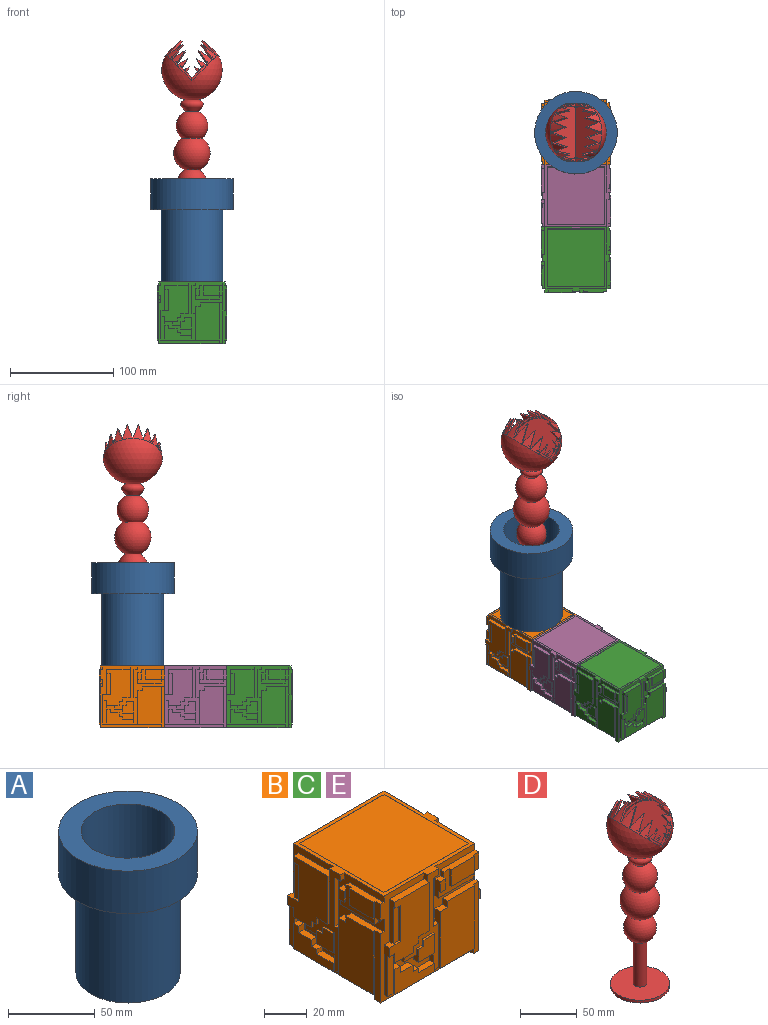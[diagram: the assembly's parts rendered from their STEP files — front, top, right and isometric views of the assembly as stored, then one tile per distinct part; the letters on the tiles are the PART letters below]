
ASSEMBLY  parts=5 mates=3
PART A: 7 faces, bbox 80x80x100 mm
  f0: cylinder r=27mm len=98mm, axis (0,0,1), area 16625.3mm2, adj f3,f6
  f1: cylinder r=40mm len=80mm, axis (0,0,1), area 7539.8mm2, adj f2,f3
  f2: plane 80x80mm, normal (0,0,-1), area 2199.1mm2, adj f1,f4
  f3: plane 80x80mm, normal (0,0,1), area 2736.3mm2, adj f0,f1
  f4: cylinder r=30mm len=70mm, axis (0,0,1), area 13194.7mm2, adj f2,f5
  f5: plane 60x60mm, normal (0,0,-1), area 2827.4mm2, adj f4
  f6: plane 54x54mm, normal (0,0,1), area 2290.2mm2, adj f0
PART B: 229 faces, bbox 67.2x63.6x60 mm
  f0: plane 64.8x62.4mm, normal (0,0,1), area 515.8mm2, adj f3,f4,f8,f9,f10,f60,f64,f67
  f1: plane 56.4x3.6mm, normal (-1,0,0), area 203mm2, adj f2,f81,f165,f210
  f2: plane 64.8x62.4mm, normal (0,0,-1), area 3625.9mm2, adj f1,f9,f10,f71,f72,f81,f142,f143
  f3: plane 27.97x26.4mm, normal (-1,0,0), area 182.8mm2, adj f0,f81,f157,f158,f161,f199
  f4: plane 31.2x30mm, normal (-1,0,0), area 331.7mm2, adj f0,f9,f149,f183,f184,f185,f186,f190
  f5: plane 3.6x2.4mm, normal (1,0,0), area 8.6mm2, adj f8,f69,f70,f75
  f6: plane 26.4x13.32mm, normal (0,-1,0), area 146.1mm2, adj f12,f28,f29,f30,f31,f32,f33,f34
  f7: plane 14.4x1.2mm, normal (-1,0,0), area 17.3mm2, adj f26,f34,f35,f74
  f8: plane 31.2x30mm, normal (0,-1,0), area 331.7mm2, adj f0,f5,f10,f44,f45,f46,f47,f51
  f9: plane 60x58.8mm, normal (0,-1,0), area 503.9mm2, adj f0,f2,f4,f11,f18,f19,f22,f26
  f10: plane 60x58.8mm, normal (1,0,0), area 503.9mm2, adj f0,f2,f8,f44,f51,f72,f75,f76
  f11: plane 28.43x3.6mm, normal (-1,0,0), area 74.5mm2, adj f9,f22,f23,f25,f26,f74
  f12: plane 12x3.6mm, normal (0,0,-1), area 31.7mm2, adj f6,f13,f24,f25,f65,f67,f73
  f13: plane 3.6x1.2mm, normal (1,0,0), area 4.3mm2, adj f12,f14,f25,f67
  f14: plane 3.6x1.2mm, normal (0,0,-1), area 4.3mm2, adj f13,f15,f25,f67
  f15: plane 3.6x1.2mm, normal (1,0,0), area 4.3mm2, adj f14,f16,f25,f67
  f16: plane 7.2x1.2mm, normal (0,0,-1), area 8.6mm2, adj f15,f17,f25,f67
  f17: plane 27.6x1.2mm, normal (1,0,0), area 33.1mm2, adj f16,f18,f25,f67
  f18: plane 22.8x3.6mm, normal (0,0,1), area 82.1mm2, adj f9,f17,f19,f25,f60
  f19: plane 24.37x3.6mm, normal (-1,0,0), area 62.8mm2, adj f9,f18,f20,f22,f25,f77
  f20: plane 3.6x1.2mm, normal (0,0,-1), area 4.3mm2, adj f19,f21,f25,f77
  f21: plane 20.77x1.2mm, normal (-1,0,0), area 24.9mm2, adj f20,f22,f25,f77
  f22: plane 7.2x3.6mm, normal (0,0,1), area 17.3mm2, adj f9,f11,f19,f21,f25,f77
  f23: plane 3.6x1.2mm, normal (0,0,-1), area 4.3mm2, adj f11,f24,f25,f74
  f24: plane 5.22x1.2mm, normal (-1,0,0), area 6.3mm2, adj f12,f23,f25,f74
  f25: plane 34.8x26.4mm, normal (0,-1,0), area 672.7mm2, adj f11,f12,f13,f14,f15,f16,f17,f18
  f26: plane 56.4x3.6mm, normal (0,0,-1), area 194.4mm2, adj f7,f9,f11,f27,f35,f43,f47,f48
  f27: plane 4.68x1.2mm, normal (1,0,0), area 5.6mm2, adj f26,f28,f35,f67
  f28: plane 10.8x3.6mm, normal (0,0,1), area 38.9mm2, adj f6,f27,f29,f35,f59
  f29: plane 3.6x2.52mm, normal (1,0,0), area 9.1mm2, adj f6,f28,f30,f35
  f30: plane 3.6x3.6mm, normal (0,0,1), area 13mm2, adj f6,f29,f31,f35
  f31: plane 3.6x3.6mm, normal (1,0,0), area 13mm2, adj f6,f30,f32,f35
  f32: plane 8.4x3.6mm, normal (0,0,1), area 30.2mm2, adj f6,f31,f33,f35
  f33: plane 3.6x3.6mm, normal (1,0,0), area 13mm2, adj f6,f32,f34,f35
  f34: plane 3.6x3.6mm, normal (0,0,1), area 13mm2, adj f6,f7,f33,f35,f73
  f35: plane 26.4x14.4mm, normal (0,-1,0), area 219.1mm2, adj f7,f26,f27,f28,f29,f30,f31,f32
  f36: plane 7.4x3.6mm, normal (-1,0,0), area 18mm2, adj f6,f37,f41,f42,f66,f67
  f37: plane 10.8x3.6mm, normal (0,0,-1), area 38.9mm2, adj f6,f36,f38,f42,f59
  f38: plane 11x1.2mm, normal (1,0,0), area 13.2mm2, adj f37,f39,f42,f67
  f39: plane 7.2x1.2mm, normal (0,0,1), area 8.6mm2, adj f38,f40,f42,f67
  f40: plane 3.6x1.2mm, normal (-1,0,0), area 4.3mm2, adj f39,f41,f42,f67
  f41: plane 3.6x1.2mm, normal (0,0,1), area 4.3mm2, adj f36,f40,f42,f67
  f42: plane 11x10.8mm, normal (0,-1,0), area 105.8mm2, adj f36,f37,f38,f39,f40,f41
  f43: plane 36x1.2mm, normal (1,0,0), area 43.2mm2, adj f26,f44,f48,f72
  f44: plane 21.6x3.6mm, normal (0,0,1), area 73.4mm2, adj f8,f10,f43,f45,f48,f72
  f45: plane 3.6x3.6mm, normal (-1,0,0), area 13mm2, adj f8,f44,f46,f48
  f46: plane 4.8x3.6mm, normal (0,0,1), area 17.3mm2, adj f8,f45,f47,f48
  f47: plane 32.4x3.6mm, normal (-1,0,0), area 56.2mm2, adj f8,f26,f46,f48,f61,f67
  f48: plane 36x22.8mm, normal (0,-1,0), area 803.5mm2, adj f26,f43,f44,f45,f46,f47
  f49: plane 15.6x1.2mm, normal (0,0,-1), area 18.7mm2, adj f50,f52,f53,f70
  f50: plane 9.6x1.2mm, normal (1,0,0), area 11.5mm2, adj f49,f51,f53,f76
  f51: plane 22.8x3.6mm, normal (0,0,1), area 73.4mm2, adj f8,f10,f50,f52,f53,f68,f70,f76
  f52: plane 9.6x1.2mm, normal (-1,0,0), area 11.5mm2, adj f49,f51,f53,f70
  f53: plane 15.6x9.6mm, normal (0,-1,0), area 149.8mm2, adj f49,f50,f51,f52
  f54: plane 3.6x1.2mm, normal (0,0,-1), area 4.3mm2, adj f55,f57,f58,f70
  f55: plane 6.25x1.2mm, normal (1,0,0), area 7.5mm2, adj f54,f56,f58,f70
  f56: plane 3.6x3.6mm, normal (0,0,1), area 13mm2, adj f8,f55,f57,f58,f68
  f57: plane 9.85x3.6mm, normal (-1,0,0), area 31.1mm2, adj f8,f54,f56,f58,f69,f70
  f58: plane 6.25x3.6mm, normal (0,-1,0), area 22.5mm2, adj f54,f55,f56,f57
  f59: plane 5.92x2.4mm, normal (-1,0,0), area 14.2mm2, adj f6,f28,f37,f67
  f60: plane 3.6x2.4mm, normal (-1,0,0), area 8.6mm2, adj f0,f9,f18,f67
  f61: plane 3.6x2.4mm, normal (0,0,1), area 8.6mm2, adj f8,f47,f62,f67
  f62: plane 27.6x2.4mm, normal (1,0,0), area 66.2mm2, adj f8,f61,f63,f67
  f63: plane 3.6x2.4mm, normal (0,0,-1), area 8.6mm2, adj f8,f62,f64,f67
  f64: plane 3.6x2.4mm, normal (1,0,0), area 8.6mm2, adj f0,f8,f63,f67
  f65: plane 3.6x2.4mm, normal (-1,0,0), area 8.6mm2, adj f6,f12,f66,f67
  f66: plane 8.38x2.4mm, normal (0,0,-1), area 20.1mm2, adj f6,f36,f65,f67
  f67: plane 56.4x22.78mm, normal (0,-1,0), area 311mm2, adj f0,f12,f13,f14,f15,f16,f17,f26
  f68: plane 3.35x2.4mm, normal (-1,0,0), area 8mm2, adj f8,f51,f56,f70
  f69: plane 22.8x2.4mm, normal (0,0,-1), area 54.7mm2, adj f5,f8,f57,f70
  f70: plane 22.8x13.2mm, normal (0,-1,0), area 116.6mm2, adj f5,f49,f51,f52,f54,f55,f57,f68
  f71: plane 3.6x2.4mm, normal (-1,0,0), area 8.6mm2, adj f2,f9,f26,f72
  f72: plane 39.6x3.6mm, normal (0,-1,0), area 142.6mm2, adj f2,f10,f43,f44,f71
  f73: plane 3.6x2.4mm, normal (1,0,0), area 8.6mm2, adj f6,f12,f34,f74
  f74: plane 23.22x3.6mm, normal (0,-1,0), area 83.6mm2, adj f7,f11,f23,f24,f26,f73
  f75: plane 3.6x2.4mm, normal (0,0,-1), area 8.6mm2, adj f5,f8,f10,f76
  f76: plane 9.6x3.6mm, normal (0,-1,0), area 34.6mm2, adj f10,f50,f51,f75
  f77: plane 20.77x3.6mm, normal (0,-1,0), area 74.8mm2, adj f19,f20,f21,f22
  f78: plane 3.6x2.4mm, normal (0,1,0), area 8.6mm2, adj f80,f140,f141,f146
  f79: plane 14.4x1.2mm, normal (0,-1,0), area 17.3mm2, adj f97,f105,f106,f145
  f80: plane 31.2x30mm, normal (1,0,0), area 331.7mm2, adj f0,f78,f81,f115,f116,f117,f118,f122
  f81: plane 66x60mm, normal (0,1,0), area 3792.6mm2, adj f0,f1,f2,f3,f80,f115,f122,f143
  f82: plane 28.43x3.6mm, normal (0,-1,0), area 74.5mm2, adj f10,f93,f94,f96,f97,f145
  f83: plane 12x3.6mm, normal (0,0,-1), area 31.7mm2, adj f84,f95,f96,f136,f138,f144,f218
  f84: plane 3.6x1.2mm, normal (0,1,0), area 4.3mm2, adj f83,f85,f96,f138
  f85: plane 3.6x1.2mm, normal (0,0,-1), area 4.3mm2, adj f84,f86,f96,f138
  f86: plane 3.6x1.2mm, normal (0,1,0), area 4.3mm2, adj f85,f87,f96,f138
  f87: plane 7.2x1.2mm, normal (0,0,-1), area 8.6mm2, adj f86,f88,f96,f138
  f88: plane 27.6x1.2mm, normal (0,1,0), area 33.1mm2, adj f87,f89,f96,f138
  f89: plane 22.8x3.6mm, normal (0,0,1), area 82.1mm2, adj f10,f88,f90,f96,f131
  f90: plane 24.37x3.6mm, normal (0,-1,0), area 62.8mm2, adj f10,f89,f91,f93,f96,f148
  f91: plane 3.6x1.2mm, normal (0,0,-1), area 4.3mm2, adj f90,f92,f96,f148
  f92: plane 20.77x1.2mm, normal (0,-1,0), area 24.9mm2, adj f91,f93,f96,f148
  f93: plane 7.2x3.6mm, normal (0,0,1), area 17.3mm2, adj f10,f82,f90,f92,f96,f148
  f94: plane 3.6x1.2mm, normal (0,0,-1), area 4.3mm2, adj f82,f95,f96,f145
  f95: plane 5.22x1.2mm, normal (0,-1,0), area 6.3mm2, adj f83,f94,f96,f145
  f96: plane 34.8x26.4mm, normal (1,0,0), area 672.7mm2, adj f82,f83,f84,f85,f86,f87,f88,f89
  f97: plane 56.4x3.6mm, normal (0,0,-1), area 194.4mm2, adj f10,f79,f82,f98,f106,f114,f118,f119
  f98: plane 4.68x1.2mm, normal (0,1,0), area 5.6mm2, adj f97,f99,f106,f138
  f99: plane 10.8x3.6mm, normal (0,0,1), area 38.9mm2, adj f98,f100,f106,f130,f218
  f100: plane 3.6x2.52mm, normal (0,1,0), area 9.1mm2, adj f99,f101,f106,f218
  f101: plane 3.6x3.6mm, normal (0,0,1), area 13mm2, adj f100,f102,f106,f218
  f102: plane 3.6x3.6mm, normal (0,1,0), area 13mm2, adj f101,f103,f106,f218
  f103: plane 8.4x3.6mm, normal (0,0,1), area 30.2mm2, adj f102,f104,f106,f218
  f104: plane 3.6x3.6mm, normal (0,1,0), area 13mm2, adj f103,f105,f106,f218
  f105: plane 3.6x3.6mm, normal (0,0,1), area 13mm2, adj f79,f104,f106,f144,f218
  f106: plane 26.4x14.4mm, normal (1,0,0), area 219.1mm2, adj f79,f97,f98,f99,f100,f101,f102,f103
  f107: plane 7.4x3.6mm, normal (0,-1,0), area 18mm2, adj f108,f112,f113,f137,f138,f218
  f108: plane 10.8x3.6mm, normal (0,0,-1), area 38.9mm2, adj f107,f109,f113,f130,f218
  f109: plane 11x1.2mm, normal (0,1,0), area 13.2mm2, adj f108,f110,f113,f138
  f110: plane 7.2x1.2mm, normal (0,0,1), area 8.6mm2, adj f109,f111,f113,f138
  f111: plane 3.6x1.2mm, normal (0,-1,0), area 4.3mm2, adj f110,f112,f113,f138
  f112: plane 3.6x1.2mm, normal (0,0,1), area 4.3mm2, adj f107,f111,f113,f138
  f113: plane 11x10.8mm, normal (1,0,0), area 105.8mm2, adj f107,f108,f109,f110,f111,f112
  f114: plane 36x1.2mm, normal (0,1,0), area 43.2mm2, adj f97,f115,f119,f143
  f115: plane 21.6x3.6mm, normal (0,0,1), area 73.4mm2, adj f80,f81,f114,f116,f119,f143
  f116: plane 3.6x3.6mm, normal (0,-1,0), area 13mm2, adj f80,f115,f117,f119
  f117: plane 4.8x3.6mm, normal (0,0,1), area 17.3mm2, adj f80,f116,f118,f119
  f118: plane 32.4x3.6mm, normal (0,-1,0), area 56.2mm2, adj f80,f97,f117,f119,f132,f138
  f119: plane 36x22.8mm, normal (1,0,0), area 803.5mm2, adj f97,f114,f115,f116,f117,f118
  f120: plane 15.6x1.2mm, normal (0,0,-1), area 18.7mm2, adj f121,f123,f124,f141
  f121: plane 9.6x1.2mm, normal (0,1,0), area 11.5mm2, adj f120,f122,f124,f147
  f122: plane 22.8x3.6mm, normal (0,0,1), area 73.4mm2, adj f80,f81,f121,f123,f124,f139,f141,f147
  f123: plane 9.6x1.2mm, normal (0,-1,0), area 11.5mm2, adj f120,f122,f124,f141
  f124: plane 15.6x9.6mm, normal (1,0,0), area 149.8mm2, adj f120,f121,f122,f123
  f125: plane 3.6x1.2mm, normal (0,0,-1), area 4.3mm2, adj f126,f128,f129,f141
  f126: plane 6.25x1.2mm, normal (0,1,0), area 7.5mm2, adj f125,f127,f129,f141
  f127: plane 3.6x3.6mm, normal (0,0,1), area 13mm2, adj f80,f126,f128,f129,f139
  f128: plane 9.85x3.6mm, normal (0,-1,0), area 31.1mm2, adj f80,f125,f127,f129,f140,f141
  f129: plane 6.25x3.6mm, normal (1,0,0), area 22.5mm2, adj f125,f126,f127,f128
  f130: plane 5.92x2.4mm, normal (0,-1,0), area 14.2mm2, adj f99,f108,f138,f218
  f131: plane 3.6x2.4mm, normal (0,-1,0), area 8.6mm2, adj f0,f10,f89,f138
  f132: plane 3.6x2.4mm, normal (0,0,1), area 8.6mm2, adj f80,f118,f133,f138
  f133: plane 27.6x2.4mm, normal (0,1,0), area 66.2mm2, adj f80,f132,f134,f138
  f134: plane 3.6x2.4mm, normal (0,0,-1), area 8.6mm2, adj f80,f133,f135,f138
  f135: plane 3.6x2.4mm, normal (0,1,0), area 8.6mm2, adj f0,f80,f134,f138
  f136: plane 3.6x2.4mm, normal (0,-1,0), area 8.6mm2, adj f83,f137,f138,f218
  f137: plane 8.38x2.4mm, normal (0,0,-1), area 20.1mm2, adj f107,f136,f138,f218
  f138: plane 56.4x22.78mm, normal (1,0,0), area 311mm2, adj f0,f83,f84,f85,f86,f87,f88,f97
  f139: plane 3.35x2.4mm, normal (0,-1,0), area 8mm2, adj f80,f122,f127,f141
  f140: plane 22.8x2.4mm, normal (0,0,-1), area 54.7mm2, adj f78,f80,f128,f141
  f141: plane 22.8x13.2mm, normal (1,0,0), area 116.6mm2, adj f78,f120,f122,f123,f125,f126,f128,f139
  f142: plane 3.6x2.4mm, normal (0,-1,0), area 8.6mm2, adj f2,f10,f97,f143
  f143: plane 39.6x3.6mm, normal (1,0,0), area 142.6mm2, adj f2,f81,f114,f115,f142
  f144: plane 3.6x2.4mm, normal (0,1,0), area 8.6mm2, adj f83,f105,f145,f218
  f145: plane 23.22x3.6mm, normal (1,0,0), area 83.6mm2, adj f79,f82,f94,f95,f97,f144
  f146: plane 3.6x2.4mm, normal (0,0,-1), area 8.6mm2, adj f78,f80,f81,f147
  f147: plane 9.6x3.6mm, normal (1,0,0), area 34.6mm2, adj f81,f121,f122,f146
  f148: plane 20.77x3.6mm, normal (1,0,0), area 74.8mm2, adj f90,f91,f92,f93
  f149: plane 3.6x2.4mm, normal (0,-1,0), area 8.6mm2, adj f4,f208,f209,f214
  f150: plane 14.4x1.2mm, normal (0,1,0), area 17.3mm2, adj f165,f173,f174,f213
  f151: plane 12x3.6mm, normal (0,0,-1), area 31.7mm2, adj f152,f163,f164,f204,f206,f212,f217
  f152: plane 3.6x1.2mm, normal (0,-1,0), area 4.3mm2, adj f151,f153,f164,f206
  f153: plane 3.6x1.2mm, normal (0,0,-1), area 4.3mm2, adj f152,f154,f164,f206
  f154: plane 3.6x1.2mm, normal (0,-1,0), area 4.3mm2, adj f153,f155,f164,f206
  f155: plane 7.2x1.2mm, normal (0,0,-1), area 8.6mm2, adj f154,f156,f164,f206
  f156: plane 27.6x1.2mm, normal (0,-1,0), area 33.1mm2, adj f155,f157,f164,f206
  f157: plane 22.8x3.6mm, normal (0,0,1), area 82.1mm2, adj f3,f156,f158,f164,f199
  f158: plane 24.37x3.6mm, normal (0,1,0), area 62.8mm2, adj f3,f157,f159,f161,f164,f216
  f159: plane 3.6x1.2mm, normal (0,0,-1), area 4.3mm2, adj f158,f160,f164,f216
  f160: plane 20.77x1.2mm, normal (0,1,0), area 24.9mm2, adj f159,f161,f164,f216
  f161: plane 7.2x3.6mm, normal (0,0,1), area 17.3mm2, adj f3,f81,f158,f160,f164,f216
  f162: plane 3.6x1.2mm, normal (0,0,-1), area 4.3mm2, adj f81,f163,f164,f213
  f163: plane 5.22x1.2mm, normal (0,1,0), area 6.3mm2, adj f151,f162,f164,f213
  f164: plane 34.8x26.4mm, normal (-1,0,0), area 672.7mm2, adj f81,f151,f152,f153,f154,f155,f156,f157
  f165: plane 56.4x3.6mm, normal (0,0,-1), area 194.4mm2, adj f1,f81,f150,f166,f174,f182,f186,f187
  f166: plane 4.68x1.2mm, normal (0,-1,0), area 5.6mm2, adj f165,f167,f174,f206
  f167: plane 10.8x3.6mm, normal (0,0,1), area 38.9mm2, adj f166,f168,f174,f198,f217
  f168: plane 3.6x2.52mm, normal (0,-1,0), area 9.1mm2, adj f167,f169,f174,f217
  f169: plane 3.6x3.6mm, normal (0,0,1), area 13mm2, adj f168,f170,f174,f217
  f170: plane 3.6x3.6mm, normal (0,-1,0), area 13mm2, adj f169,f171,f174,f217
  f171: plane 8.4x3.6mm, normal (0,0,1), area 30.2mm2, adj f170,f172,f174,f217
  f172: plane 3.6x3.6mm, normal (0,-1,0), area 13mm2, adj f171,f173,f174,f217
  f173: plane 3.6x3.6mm, normal (0,0,1), area 13mm2, adj f150,f172,f174,f212,f217
  f174: plane 26.4x14.4mm, normal (-1,0,0), area 219.1mm2, adj f150,f165,f166,f167,f168,f169,f170,f171
  f175: plane 7.4x3.6mm, normal (0,1,0), area 18mm2, adj f176,f180,f181,f205,f206,f217
  f176: plane 10.8x3.6mm, normal (0,0,-1), area 38.9mm2, adj f175,f177,f181,f198,f217
  f177: plane 11x1.2mm, normal (0,-1,0), area 13.2mm2, adj f176,f178,f181,f206
  f178: plane 7.2x1.2mm, normal (0,0,1), area 8.6mm2, adj f177,f179,f181,f206
  f179: plane 3.6x1.2mm, normal (0,1,0), area 4.3mm2, adj f178,f180,f181,f206
  f180: plane 3.6x1.2mm, normal (0,0,1), area 4.3mm2, adj f175,f179,f181,f206
  f181: plane 11x10.8mm, normal (-1,0,0), area 105.8mm2, adj f175,f176,f177,f178,f179,f180
  f182: plane 36x1.2mm, normal (0,-1,0), area 43.2mm2, adj f165,f183,f187,f211
  f183: plane 21.6x3.6mm, normal (0,0,1), area 73.4mm2, adj f4,f9,f182,f184,f187,f211
  f184: plane 3.6x3.6mm, normal (0,1,0), area 13mm2, adj f4,f183,f185,f187
  f185: plane 4.8x3.6mm, normal (0,0,1), area 17.3mm2, adj f4,f184,f186,f187
  f186: plane 32.4x3.6mm, normal (0,1,0), area 56.2mm2, adj f4,f165,f185,f187,f200,f206
  f187: plane 36x22.8mm, normal (-1,0,0), area 803.5mm2, adj f165,f182,f183,f184,f185,f186
  f188: plane 15.6x1.2mm, normal (0,0,-1), area 18.7mm2, adj f189,f191,f192,f209
  f189: plane 9.6x1.2mm, normal (0,-1,0), area 11.5mm2, adj f188,f190,f192,f215
  f190: plane 22.8x3.6mm, normal (0,0,1), area 73.4mm2, adj f4,f9,f189,f191,f192,f207,f209,f215
  f191: plane 9.6x1.2mm, normal (0,1,0), area 11.5mm2, adj f188,f190,f192,f209
  f192: plane 15.6x9.6mm, normal (-1,0,0), area 149.8mm2, adj f188,f189,f190,f191
  f193: plane 3.6x1.2mm, normal (0,0,-1), area 4.3mm2, adj f194,f196,f197,f209
  f194: plane 6.25x1.2mm, normal (0,-1,0), area 7.5mm2, adj f193,f195,f197,f209
  f195: plane 3.6x3.6mm, normal (0,0,1), area 13mm2, adj f4,f194,f196,f197,f207
  f196: plane 9.85x3.6mm, normal (0,1,0), area 31.1mm2, adj f4,f193,f195,f197,f208,f209
  f197: plane 6.25x3.6mm, normal (-1,0,0), area 22.5mm2, adj f193,f194,f195,f196
  f198: plane 5.92x2.4mm, normal (0,1,0), area 14.2mm2, adj f167,f176,f206,f217
  f199: plane 3.6x2.4mm, normal (0,1,0), area 8.6mm2, adj f0,f3,f157,f206
  f200: plane 3.6x2.4mm, normal (0,0,1), area 8.6mm2, adj f4,f186,f201,f206
  f201: plane 27.6x2.4mm, normal (0,-1,0), area 66.2mm2, adj f4,f200,f202,f206
  f202: plane 3.6x2.4mm, normal (0,0,-1), area 8.6mm2, adj f4,f201,f203,f206
  f203: plane 3.6x2.4mm, normal (0,-1,0), area 8.6mm2, adj f0,f4,f202,f206
  f204: plane 3.6x2.4mm, normal (0,1,0), area 8.6mm2, adj f151,f205,f206,f217
  f205: plane 8.38x2.4mm, normal (0,0,-1), area 20.1mm2, adj f175,f204,f206,f217
  f206: plane 56.4x22.78mm, normal (-1,0,0), area 311mm2, adj f0,f151,f152,f153,f154,f155,f156,f165
  f207: plane 3.35x2.4mm, normal (0,1,0), area 8mm2, adj f4,f190,f195,f209
  f208: plane 22.8x2.4mm, normal (0,0,-1), area 54.7mm2, adj f4,f149,f196,f209
  f209: plane 22.8x13.2mm, normal (-1,0,0), area 116.6mm2, adj f149,f188,f190,f191,f193,f194,f196,f207
  f210: plane 3.6x2.4mm, normal (0,1,0), area 8.6mm2, adj f1,f2,f165,f211
  f211: plane 39.6x3.6mm, normal (-1,0,0), area 142.6mm2, adj f2,f9,f182,f183,f210
  f212: plane 3.6x2.4mm, normal (0,-1,0), area 8.6mm2, adj f151,f173,f213,f217
  f213: plane 23.22x3.6mm, normal (-1,0,0), area 83.6mm2, adj f81,f150,f162,f163,f165,f212
  f214: plane 3.6x2.4mm, normal (0,0,-1), area 8.6mm2, adj f4,f9,f149,f215
  f215: plane 9.6x3.6mm, normal (-1,0,0), area 34.6mm2, adj f9,f189,f190,f214
  f216: plane 20.77x3.6mm, normal (-1,0,0), area 74.8mm2, adj f158,f159,f160,f161
  f217: plane 26.4x13.32mm, normal (-1,0,0), area 146.1mm2, adj f151,f167,f168,f169,f170,f171,f172,f173
  f218: plane 26.4x13.32mm, normal (1,0,0), area 146.1mm2, adj f83,f99,f100,f101,f102,f103,f104,f105
  f219: plane 55.8x55mm, normal (-1,0,0), area 3069mm2, adj f220,f226,f227,f228
  f220: plane 55.82x55mm, normal (0,1,0), area 3070.1mm2, adj f219,f221,f227,f228
  f221: plane 55.8x55mm, normal (1,0,0), area 3069mm2, adj f220,f226,f227,f228
  f222: plane 56x55mm, normal (1,0,0), area 3080mm2, adj f0,f223,f225,f227
  f223: plane 56x55mm, normal (0,1,0), area 3080mm2, adj f0,f222,f224,f227
  f224: plane 56x55mm, normal (-1,0,0), area 3080mm2, adj f0,f223,f225,f227
  f225: plane 56x55mm, normal (0,-1,0), area 3080mm2, adj f0,f222,f224,f227
  f226: plane 55.82x55mm, normal (0,-1,0), area 3070.1mm2, adj f219,f221,f227,f228
  f227: plane 56x56mm, normal (0,0,1), area 21.2mm2, adj f219,f220,f221,f222,f223,f224,f225,f226
  f228: plane 55.82x55.8mm, normal (0,0,1), area 3114.8mm2, adj f219,f220,f221,f226
PART C: same geometry as B
PART D: 139 faces, bbox 58.7x58.7x210.3 mm
  f0: plane 1.91x1.91mm, normal (0.71,0,-0.71), area 0.2mm2, adj f29,f30,f124
  f1: plane 4.07x3.21mm, normal (0.71,0,-0.71), area 0.5mm2, adj f24,f25,f124
  f2: plane 6.11x2.32mm, normal (0.71,0,-0.71), area 0.2mm2, adj f19,f20,f124
  f3: plane 6.11x2.32mm, normal (0.71,0,-0.71), area 0.2mm2, adj f37,f41,f124
  f4: plane 4.07x3.21mm, normal (0.71,0,-0.71), area 0.5mm2, adj f46,f47,f124
  f5: plane 1.91x1.91mm, normal (0.71,0,-0.71), area 0.2mm2, adj f51,f52,f124
  f6: cylinder r=26.47mm len=13.98mm, axis (-0.71,0,0.71), area 86mm2, adj f8,f9,f10
  f7: cylinder r=28.47mm len=21.38mm, axis (-0.71,0,0.71), area 214.8mm2, adj f8,f9,f10,f19,f21,f38,f41,f43
  f8: plane 14.47x13.79mm, normal (-0.05,-0.95,0.31), area 37.4mm2, adj f6,f7,f9,f10
  f9: plane 15.05x13.21mm, normal (-0.31,0.95,0.05), area 37.4mm2, adj f6,f7,f8,f10
  f10: plane 56.95x23.72mm, normal (-0.71,0,0.71), area 175.8mm2, adj f6,f7,f8,f9,f11,f12,f13,f14
  f11: cylinder r=28.47mm len=14.3mm, axis (0.71,0,-0.71), area 35.2mm2, adj f10,f52,f76,f124
  f12: cylinder r=28.47mm len=3.9mm, axis (0.71,0,-0.71), area 7.8mm2, adj f10,f47,f51,f53,f124
  f13: cylinder r=28.47mm len=3.09mm, axis (0.71,0,-0.71), area 7mm2, adj f10,f37,f46,f48,f124
  f14: cylinder r=28.47mm len=14.3mm, axis (0.71,0,-0.71), area 35.2mm2, adj f10,f30,f79,f124
  f15: cylinder r=28.47mm len=3.9mm, axis (0.71,0,-0.71), area 7.8mm2, adj f10,f25,f29,f31,f124
  f16: cylinder r=28.47mm len=3.09mm, axis (0.71,0,-0.71), area 7mm2, adj f10,f20,f24,f26,f124
  f17: cylinder r=25.47mm len=50.95mm, axis (0.71,0,-0.71), area 180.5mm2, adj f10,f60,f61,f64
  f18: cylinder r=23.83mm len=14.42mm, axis (-0.71,0,0.71), area 68mm2, adj f10,f21,f22
  f19: plane 0.04x0.02mm, normal (0.25,-0.94,0.25), area 0mm2, adj f2,f7,f21
  f20: cylinder r=25.63mm len=15.97mm, axis (-0.71,0,0.71), area 81.3mm2, adj f2,f10,f16,f21,f22
  f21: plane 15.29x11.26mm, normal (0.17,-0.83,0.54), area 30mm2, adj f7,f10,f18,f19,f20,f22
  f22: plane 14.19x10.64mm, normal (-0.54,0.83,-0.17), area 29.9mm2, adj f10,f18,f20,f21
  f23: cylinder r=21.18mm len=14.02mm, axis (-0.71,0,0.71), area 52mm2, adj f10,f26,f27
  f24: plane 0.11x0.07mm, normal (0.46,-0.75,0.46), area 0mm2, adj f1,f16,f26
  f25: cylinder r=22.78mm len=15.68mm, axis (-0.71,0,0.71), area 63.6mm2, adj f1,f10,f15,f26,f27
  f26: plane 14.19x9.14mm, normal (0.36,-0.6,0.72), area 23.5mm2, adj f10,f16,f23,f24,f25,f27
  f27: plane 12.8x8.41mm, normal (-0.72,0.6,-0.36), area 23.3mm2, adj f10,f23,f25,f26
  f28: cylinder r=15.88mm len=10.64mm, axis (-0.71,0,0.71), area 26.5mm2, adj f10,f31,f32
  f29: plane 0.11x0.11mm, normal (0.62,-0.48,0.62), area 0mm2, adj f0,f15,f31
  f30: cylinder r=17.08mm len=12.39mm, axis (-0.71,0,0.71), area 31.9mm2, adj f0,f10,f14,f31,f32
  f31: plane 10.82x6.41mm, normal (0.47,-0.3,0.83), area 12.7mm2, adj f10,f15,f28,f29,f30,f32
  f32: plane 9.16x5.5mm, normal (-0.83,0.3,-0.47), area 12.5mm2, adj f10,f28,f30,f31
  f33: cylinder r=10.59mm len=6.49mm, axis (-0.71,0,0.71), area 9.6mm2, adj f10,f35,f36
  f34: cylinder r=11.39mm len=6.49mm, axis (-0.71,0,0.71), area 9.6mm2, adj f10,f35,f36
  f35: plane 5.41x3.16mm, normal (0.5,0.05,0.86), area 5mm2, adj f10,f33,f34,f36
  f36: plane 5.41x3.17mm, normal (-0.86,-0.05,-0.5), area 5mm2, adj f10,f33,f34,f35
  f37: cylinder r=25.63mm len=15.97mm, axis (-0.71,0,0.71), area 81.3mm2, adj f3,f10,f13,f38,f39
  f38: plane 15.29x11.26mm, normal (0.17,0.83,0.54), area 30mm2, adj f7,f10,f37,f39,f40,f41
  f39: plane 14.19x10.64mm, normal (-0.54,-0.83,-0.17), area 29.9mm2, adj f10,f37,f38,f40
  f40: cylinder r=23.83mm len=14.42mm, axis (-0.71,0,0.71), area 68mm2, adj f10,f38,f39
  f41: plane 0.04x0.02mm, normal (0.25,0.94,0.25), area 0mm2, adj f3,f7,f38
  f42: cylinder r=26.47mm len=13.98mm, axis (-0.71,0,0.71), area 86mm2, adj f10,f43,f44
  f43: plane 14.47x13.79mm, normal (-0.05,0.95,0.31), area 37.4mm2, adj f7,f10,f42,f44
  f44: plane 15.05x13.21mm, normal (-0.31,-0.95,0.05), area 37.4mm2, adj f7,f10,f42,f43
  f45: cylinder r=21.18mm len=14.02mm, axis (-0.71,0,0.71), area 52mm2, adj f10,f48,f49
  f46: plane 0.11x0.07mm, normal (0.46,0.75,0.46), area 0mm2, adj f4,f13,f48
  f47: cylinder r=22.78mm len=15.68mm, axis (-0.71,0,0.71), area 63.6mm2, adj f4,f10,f12,f48,f49
  f48: plane 14.19x9.14mm, normal (0.36,0.6,0.72), area 23.5mm2, adj f10,f13,f45,f46,f47,f49
  f49: plane 12.8x8.41mm, normal (-0.72,-0.6,-0.36), area 23.3mm2, adj f10,f45,f47,f48
  f50: cylinder r=15.88mm len=10.64mm, axis (-0.71,0,0.71), area 26.5mm2, adj f10,f53,f54
  f51: plane 0.11x0.11mm, normal (0.62,0.48,0.62), area 0mm2, adj f5,f12,f53
  f52: cylinder r=17.08mm len=12.39mm, axis (-0.71,0,0.71), area 31.9mm2, adj f5,f10,f11,f53,f54
  f53: plane 10.82x6.41mm, normal (0.47,0.3,0.83), area 12.7mm2, adj f10,f12,f50,f51,f52,f54
  f54: plane 9.16x5.5mm, normal (-0.83,-0.3,-0.47), area 12.5mm2, adj f10,f50,f52,f53
  f55: cylinder r=10.59mm len=6.49mm, axis (-0.71,0,0.71), area 9.6mm2, adj f10,f57,f58
  f56: cylinder r=11.39mm len=6.49mm, axis (-0.71,0,0.71), area 9.6mm2, adj f10,f57,f58
  f57: plane 5.41x3.16mm, normal (0.5,-0.05,0.86), area 5mm2, adj f10,f55,f56,f58
  f58: plane 5.41x3.17mm, normal (-0.86,0.05,-0.5), area 5mm2, adj f10,f55,f56,f57
  f59: plane 50.95x23.01mm, normal (0.71,0,0.71), area 1373.7mm2, adj f64,f82,f135,f136,f137,f138
  f60: plane 1.41x1.41mm, normal (0.71,0,0.71), area 0.5mm2, adj f17,f63,f64
  f61: plane 1.41x1.41mm, normal (0.71,0,0.71), area 0.5mm2, adj f17,f62,f64
  f62: cylinder r=25.47mm len=2.83mm, axis (-0.71,0,-0.71), area 2.1mm2, adj f61,f64,f137
  f63: cylinder r=25.47mm len=2.83mm, axis (-0.71,0,-0.71), area 2.1mm2, adj f60,f64,f135
  f64: plane 50.95x23.01mm, normal (-0.71,0,0.71), area 1373.7mm2, adj f17,f59,f60,f61,f62,f63
  f65: plane 1.91x1.91mm, normal (-0.71,0,-0.71), area 0.2mm2, adj f116,f117,f124
  f66: plane 4.07x3.21mm, normal (-0.71,0,-0.71), area 0.5mm2, adj f111,f112,f124
  f67: plane 6.11x2.32mm, normal (-0.71,0,-0.71), area 0.2mm2, adj f102,f106,f124
  f68: plane 6.11x2.32mm, normal (-0.71,0,-0.71), area 0.2mm2, adj f84,f85,f124
  f69: plane 4.07x3.21mm, normal (-0.71,0,-0.71), area 0.5mm2, adj f89,f90,f124
  f70: cylinder r=26.47mm len=13.98mm, axis (0.71,0,0.71), area 86mm2, adj f73,f74,f75
  f71: plane 1.91x1.91mm, normal (-0.71,0,-0.71), area 0.2mm2, adj f94,f95,f124
  f72: cylinder r=28.47mm len=21.38mm, axis (0.71,0,0.71), area 214.8mm2, adj f73,f74,f75,f84,f86,f103,f106,f108
  f73: plane 14.47x13.79mm, normal (0.05,-0.95,0.31), area 37.4mm2, adj f70,f72,f74,f75
  f74: plane 15.05x13.21mm, normal (0.31,0.95,0.05), area 37.4mm2, adj f70,f72,f73,f75
  f75: plane 56.95x23.72mm, normal (0.71,0,0.71), area 175.8mm2, adj f10,f70,f72,f73,f74,f76,f77,f78
  f76: cylinder r=28.47mm len=14.3mm, axis (-0.71,0,-0.71), area 35.2mm2, adj f11,f75,f117,f124
  f77: cylinder r=28.47mm len=3.9mm, axis (-0.71,0,-0.71), area 7.8mm2, adj f75,f112,f116,f118,f124
  f78: cylinder r=28.47mm len=3.09mm, axis (-0.71,0,-0.71), area 7mm2, adj f75,f102,f111,f113,f124
  f79: cylinder r=28.47mm len=14.3mm, axis (-0.71,0,-0.71), area 35.2mm2, adj f14,f75,f95,f124
  f80: cylinder r=28.47mm len=3.9mm, axis (-0.71,0,-0.71), area 7.8mm2, adj f75,f90,f94,f96,f124
  f81: cylinder r=28.47mm len=3.09mm, axis (-0.71,0,-0.71), area 7mm2, adj f75,f85,f89,f91,f124
  f82: cylinder r=25.47mm len=50.95mm, axis (-0.71,0,-0.71), area 180.5mm2, adj f59,f75,f136,f138
  f83: cylinder r=23.83mm len=14.42mm, axis (0.71,0,0.71), area 68mm2, adj f75,f86,f87
  f84: plane 0.04x0.02mm, normal (-0.25,-0.94,0.25), area 0mm2, adj f68,f72,f86
  f85: cylinder r=25.63mm len=15.97mm, axis (0.71,0,0.71), area 81.3mm2, adj f68,f75,f81,f86,f87
  f86: plane 15.29x11.26mm, normal (-0.17,-0.83,0.54), area 30mm2, adj f72,f75,f83,f84,f85,f87
  f87: plane 14.19x10.64mm, normal (0.54,0.83,-0.17), area 29.9mm2, adj f75,f83,f85,f86
  f88: cylinder r=21.18mm len=14.02mm, axis (0.71,0,0.71), area 52mm2, adj f75,f91,f92
  f89: plane 0.11x0.07mm, normal (-0.46,-0.75,0.46), area 0mm2, adj f69,f81,f91
  f90: cylinder r=22.78mm len=15.68mm, axis (0.71,0,0.71), area 63.6mm2, adj f69,f75,f80,f91,f92
  f91: plane 14.19x9.14mm, normal (-0.36,-0.6,0.72), area 23.5mm2, adj f75,f81,f88,f89,f90,f92
  f92: plane 12.8x8.41mm, normal (0.72,0.6,-0.36), area 23.3mm2, adj f75,f88,f90,f91
  f93: cylinder r=15.88mm len=10.64mm, axis (0.71,0,0.71), area 26.5mm2, adj f75,f96,f97
  f94: plane 0.11x0.11mm, normal (-0.62,-0.48,0.62), area 0mm2, adj f71,f80,f96
  f95: cylinder r=17.08mm len=12.39mm, axis (0.71,0,0.71), area 31.9mm2, adj f71,f75,f79,f96,f97
  f96: plane 10.82x6.41mm, normal (-0.47,-0.3,0.83), area 12.7mm2, adj f75,f80,f93,f94,f95,f97
  f97: plane 9.16x5.5mm, normal (0.83,0.3,-0.47), area 12.5mm2, adj f75,f93,f95,f96
  f98: cylinder r=10.59mm len=6.49mm, axis (0.71,0,0.71), area 9.6mm2, adj f75,f100,f101
  f99: cylinder r=11.39mm len=6.49mm, axis (0.71,0,0.71), area 9.6mm2, adj f75,f100,f101
  f100: plane 5.41x3.16mm, normal (-0.5,0.05,0.86), area 5mm2, adj f75,f98,f99,f101
  f101: plane 5.41x3.17mm, normal (0.86,-0.05,-0.5), area 5mm2, adj f75,f98,f99,f100
  f102: cylinder r=25.63mm len=15.97mm, axis (0.71,0,0.71), area 81.3mm2, adj f67,f75,f78,f103,f104
  f103: plane 15.29x11.26mm, normal (-0.17,0.83,0.54), area 30mm2, adj f72,f75,f102,f104,f105,f106
  f104: plane 14.19x10.64mm, normal (0.54,-0.83,-0.17), area 29.9mm2, adj f75,f102,f103,f105
  f105: cylinder r=23.83mm len=14.42mm, axis (0.71,0,0.71), area 68mm2, adj f75,f103,f104
  f106: plane 0.04x0.02mm, normal (-0.25,0.94,0.25), area 0mm2, adj f67,f72,f103
  f107: cylinder r=26.47mm len=13.98mm, axis (0.71,0,0.71), area 86mm2, adj f75,f108,f109
  f108: plane 14.47x13.79mm, normal (0.05,0.95,0.31), area 37.4mm2, adj f72,f75,f107,f109
  f109: plane 15.05x13.21mm, normal (0.31,-0.95,0.05), area 37.4mm2, adj f72,f75,f107,f108
  f110: cylinder r=21.18mm len=14.02mm, axis (0.71,0,0.71), area 52mm2, adj f75,f113,f114
  f111: plane 0.11x0.07mm, normal (-0.46,0.75,0.46), area 0mm2, adj f66,f78,f113
  f112: cylinder r=22.78mm len=15.68mm, axis (0.71,0,0.71), area 63.6mm2, adj f66,f75,f77,f113,f114
  f113: plane 14.19x9.14mm, normal (-0.36,0.6,0.72), area 23.5mm2, adj f75,f78,f110,f111,f112,f114
  f114: plane 12.8x8.41mm, normal (0.72,-0.6,-0.36), area 23.3mm2, adj f75,f110,f112,f113
  f115: cylinder r=15.88mm len=10.64mm, axis (0.71,0,0.71), area 26.5mm2, adj f75,f118,f119
  f116: plane 0.11x0.11mm, normal (-0.62,0.48,0.62), area 0mm2, adj f65,f77,f118
  f117: cylinder r=17.08mm len=12.39mm, axis (0.71,0,0.71), area 31.9mm2, adj f65,f75,f76,f118,f119
  f118: plane 10.82x6.41mm, normal (-0.47,0.3,0.83), area 12.7mm2, adj f75,f77,f115,f116,f117,f119
  f119: plane 9.16x5.5mm, normal (0.83,-0.3,-0.47), area 12.5mm2, adj f75,f115,f117,f118
  f120: cylinder r=10.59mm len=6.49mm, axis (0.71,0,0.71), area 9.6mm2, adj f75,f122,f123
  f121: cylinder r=11.39mm len=6.49mm, axis (0.71,0,0.71), area 9.6mm2, adj f75,f122,f123
  f122: plane 5.41x3.16mm, normal (-0.5,-0.05,0.86), area 5mm2, adj f75,f120,f121,f123
  f123: plane 5.41x3.17mm, normal (0.86,0.05,-0.5), area 5mm2, adj f75,f120,f121,f122
  f124: sphere r=29.34mm, area 6593.4mm2, adj f0,f1,f2,f3,f4,f5,f7,f11
  f125: cylinder r=26mm len=52mm, axis (0,0,1), area 490.1mm2, adj f126,f127
  f126: plane 52x52mm, normal (0,0,-1), area 2073.5mm2, adj f125,f128
  f127: plane 52x52mm, normal (0,0,1), area 2010.6mm2, adj f125,f130
  f128: cylinder r=4mm len=8mm, axis (0,0,1), area 201.1mm2, adj f126,f129
  f129: plane 8x8mm, normal (0,0,-1), area 50.3mm2, adj f128
  f130: cylinder r=6mm len=47.32mm, axis (0,0,-1), area 1784mm2, adj f127,f131
  f131: sphere r=14.56mm, area 2378.6mm2, adj f130,f132
  f132: sphere r=17.64mm, area 3413.9mm2, adj f131,f133
  f133: sphere r=15.34mm, area 2494.2mm2, adj f132,f134
  f134: revolved ~21.8x21.8mm, area 875.7mm2, adj f124,f133
  f135: cylinder r=25.47mm len=2.83mm, axis (0.71,0,-0.71), area 2.1mm2, adj f59,f63,f136
  f136: plane 1.41x1.41mm, normal (-0.71,0,0.71), area 0.5mm2, adj f59,f82,f135
  f137: cylinder r=25.47mm len=2.83mm, axis (0.71,0,-0.71), area 2.1mm2, adj f59,f62,f138
  f138: plane 1.41x1.41mm, normal (-0.71,0,0.71), area 0.5mm2, adj f59,f82,f137
PART E: same geometry as B
PLACE A t=(-26.71,128.48,15.85)mm
PLACE B rot(axis=(0,0,1),180deg) t=(-26.71,157.44,-114.15)mm
PLACE C t=(-26.71,-22.56,-114.15)mm
PLACE D t=(-26.71,128.48,-0.15)mm
PLACE E t=(-26.71,37.44,-114.15)mm
MATE fastened D.f125 <-> A.f0  axis (0,0,1) through (-26.71,128.48,-49.15)mm
MATE fastened E.f0 <-> C.f0  axis (0,0,1) through (-56.71,37.44,-84.15)mm
MATE fastened B.f0 <-> E.f0  axis (0,0,1) through (-56.71,97.44,-84.15)mm
